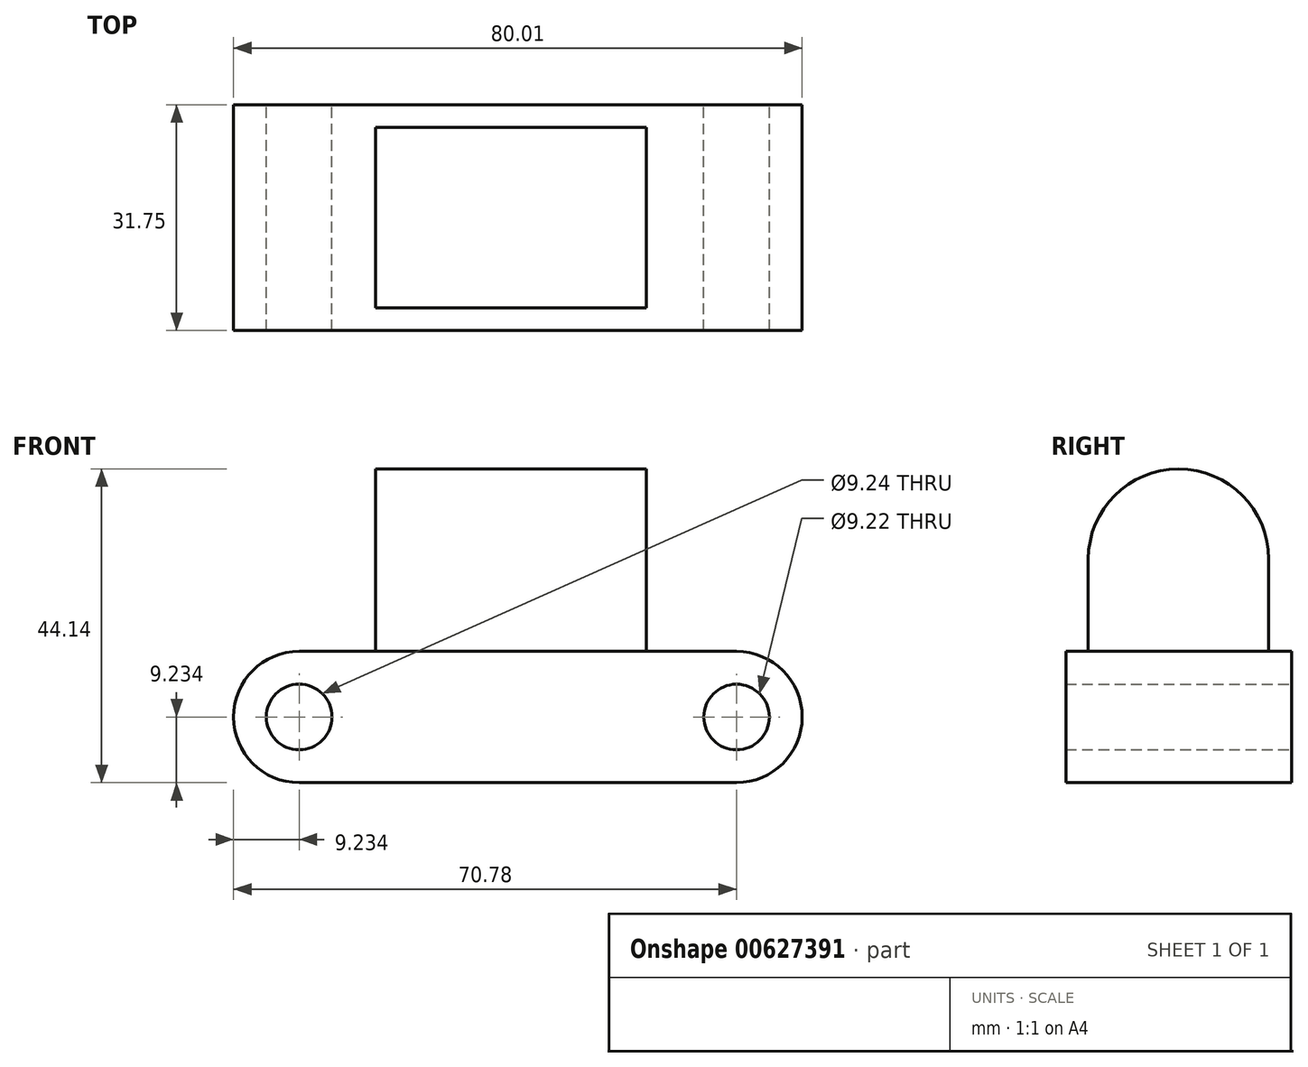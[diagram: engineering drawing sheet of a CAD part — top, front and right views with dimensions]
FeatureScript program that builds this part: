
annotation { "Feature Type Name" : "Feature", "Feature Type Description" : "" }
export const myFeature = defineFeature(function(context is Context, id is Id, definition is map)
    precondition{}
    {
        {
            var Q0;
            Q0=qCreatedBy(makeId("Front.planeOp"),FACE);
            var sketch = newSketch(context, id + "F0", { "sketchPlane" : qUnion([Q0])});
            skLineSegment(sketch, "E0.bottom", {"start": v(0, 0) * mm, "end": v(-61.55, 0) * mm});
            skLineSegment(sketch, "E0.top", {"start": v(0, 18.47) * mm, "end": v(-61.55, 18.47) * mm});
            skArc(sketch, "E1", {"start": v(-61.55, 18.47) * mm, "mid": v(-70.78, 9.23) * mm, "end": v(-61.55, 0) * mm});
            skCircle(sketch, "E2", {"center": v(-61.55, 9.23) * mm, "radius": 4.62 * mm});
            skCircle(sketch, "E3", {"center": v(0, 9.23) * mm, "radius": 4.61 * mm});
            skCircle(sketch, "E4", {"center": v(0, 9.23) * mm, "radius": 9.23 * mm});
            skLineSegment(sketch, "E5", {"start": v(0, 9.23) * mm, "end": v(0, 31.46) * mm});
            skSolve(sketch);
        }
        {
            var Q0;
            Q0 = qSketchRegion(id + "F0", true);
            extrude(context, id + "F1", {"entities" : qUnion([Q0]), "depth" : 31.75 * mm, "offsetDistance" : 25.4 * mm});
        }
        {
            var Q0;
            Q0=makeQuery(id+"F1.opExtrude","SWEPT_FACE",FACE,{"disambiguationData":[OSD([sQuery(id+"F0.wireOp",EDGE,"E0.top")])]});
            var sketch = newSketch(context, id + "F2", { "sketchPlane" : qUnion([Q0])});
            skLineSegment(sketch, "E6", {"start": v(-50.8, -15.88) * mm, "end": v(-50.8, -28.58) * mm});
            skLineSegment(sketch, "E7", {"start": v(-50.8, -15.88) * mm, "end": v(-50.8, -3.18) * mm});
            skLineSegment(sketch, "E8", {"start": v(-50.8, -28.58) * mm, "end": v(-50.8, -3.18) * mm});
            skLineSegment(sketch, "E9.0", {"start": v(-12.7, -28.58) * mm, "end": v(-12.7, -3.18) * mm});
            skLineSegment(sketch, "E10", {"start": v(-12.7, -3.18) * mm, "end": v(-50.8, -3.18) * mm});
            skLineSegment(sketch, "E11", {"start": v(-12.7, -28.58) * mm, "end": v(-50.8, -28.58) * mm});
            skSolve(sketch);
        }
        {
            var Q0;
            Q0 = qSketchRegion(id + "F2", true);
            extrude(context, id + "F3", {"entities" : qUnion([Q0]), "operationType" : NewBodyOperationType.ADD, "depth" : 12.98 * mm, "offsetDistance" : 25.4 * mm});
        }
        {
            var Q0;
            Q0=makeQuery(id+"F3.opExtrude","SWEPT_FACE",FACE,{"disambiguationData":[OSD([sQuery(id+"F2.wireOp",EDGE,"E9.0")])]});
            var sketch = newSketch(context, id + "F4", { "sketchPlane" : qUnion([Q0])});
            skCircle(sketch, "E12", {"center": v(-15.88, 31.45) * mm, "radius": 12.7 * mm});
            skSolve(sketch);
        }
        {
            var Q0;
            Q0 = qSketchRegion(id + "F4", true);
            extrude(context, id + "F5", {"entities" : qUnion([Q0]), "operationType" : NewBodyOperationType.ADD, "oppositeDirection" : true, "depth" : 38.1 * mm, "offsetDistance" : 25.4 * mm});
        }
    });
